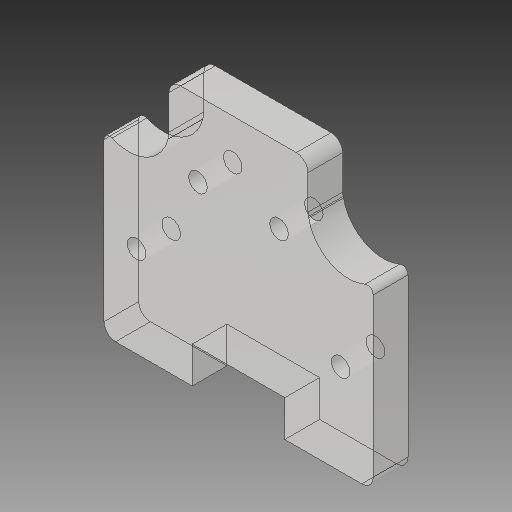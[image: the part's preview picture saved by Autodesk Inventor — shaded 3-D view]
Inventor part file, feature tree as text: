
AUTODESK INVENTOR PART (.ipt)
format: ipt  version: 2018 (Build 220112000, 112)  size: 196,608 bytes
history: native  units: in
note: dims shown in document units (in); Inventor stores cm internally (conversion verified against a paired STEP export)
features: extrude x4, sketch x4, reference x3, other x3, fillet x2, plane x1
ambient origin geometry x8: Origin, YZ Plane, XZ Plane, XY Plane, X Axis, Y Axis, Z Axis, Center Point
bodies: Solid1 (feature_tree)
feature tree (17):
  extrude  "Extrusion1"  Depth=0.2362in TaperAngle=0.0deg
  extrude  "Extrusion2"  Depth=0.0787in
  fillet  "Fillet1"  Radius=0.315in
  fillet  "Fillet2"  [1 undecoded]
  extrude  "Extrusion3"  TaperAngle=0.0deg  [1 undecoded]
  sketch  "Sketch4"  dims[d10=0.3937in d11=0.0in d12=0.3937in d13=0.0in]
  plane  "Work Plane1"
  extrude  "Extrusion4"  Depth=0.3937in TaperAngle=0.0deg
  sketch  "Sketch1"  dims[d0=0.2362in d1=0.0in d2=0.2362in d3=0.0in]
  sketch  "Sketch2"  dims[d4=0.0394in d5=0.0787in d6=0.315in d7=180.0deg]
  reference  "Reference1"
  reference  "Reference2"
  sketch  "Sketch3"  dims[d8=0.6299in d9=0.0in]
  reference  "Reference3"
  other  "<userpath>\OneDrive\Inventor\Beast 3D Printer\Hotend Mount Assembly.iam"
  other  "Hotend Mount Assembly.iam"
  other  "Hotend Slide Part 2:1"
note: 2 required parameter values undecoded (feature->parameter linkage not recoverable at this tier; creation-order binding heuristic only, values carry confidence <= 0.55)
